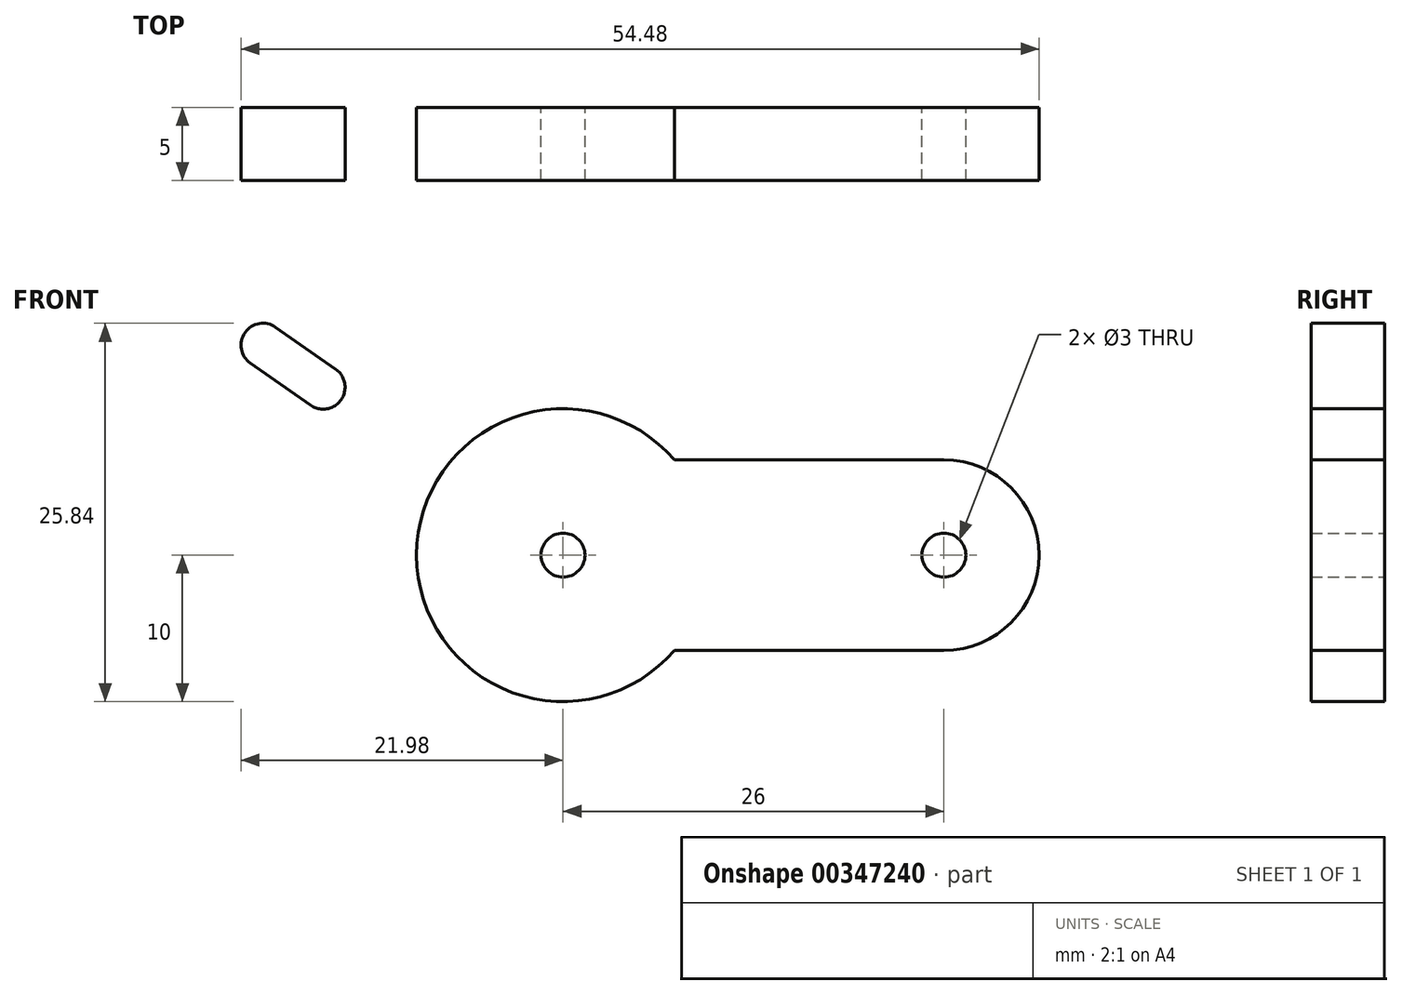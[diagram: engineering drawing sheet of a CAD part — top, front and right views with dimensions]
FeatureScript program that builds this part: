
annotation { "Feature Type Name" : "Feature", "Feature Type Description" : "" }
export const myFeature = defineFeature(function(context is Context, id is Id, definition is map)
    precondition{}
    {
        {
            var Q0;
            Q0=qCreatedBy(makeId("Front.planeOp"),FACE);
            var sketch = newSketch(context, id + "F0", { "sketchPlane" : qUnion([Q0])});
            skLineSegment(sketch, "E0", {"start": v(1.5, 0) * mm, "end": v(26, 0) * mm});
            skLineSegment(sketch, "E1", {"start": v(-1.23, 0.86) * mm, "end": v(-16.38, 11.47) * mm});
            skLineSegment(sketch, "E2", {"start": v(-16.38, 11.47) * mm, "end": v(-20.48, 14.34) * mm});
            skCircle(sketch, "E3", {"center": v(0, 0) * mm, "radius": 1.5 * mm});
            skCircle(sketch, "E4", {"center": v(26, 0) * mm, "radius": 1.5 * mm});
            skArc(sketch, "E5.0.startCap", {"start": v(-15.52, 12.7) * mm, "mid": v(-15.15, 10.61) * mm, "end": v(-17.24, 10.24) * mm});
            skArc(sketch, "E5.0.endCap", {"start": v(-21.34, 13.11) * mm, "mid": v(-21.7, 15.2) * mm, "end": v(-19.62, 15.57) * mm});
            skLineSegment(sketch, "E5.0.left", {"start": v(-17.24, 10.24) * mm, "end": v(-21.34, 13.11) * mm});
            skLineSegment(sketch, "E5.0.right", {"start": v(-15.52, 12.7) * mm, "end": v(-19.62, 15.57) * mm});
            skLineSegment(sketch, "E6.0.left", {"start": v(-9.95, -0.97) * mm, "end": v(-20.11, 6.15) * mm});
            skCircle(sketch, "E7", {"center": v(0, 0) * mm, "radius": 10 * mm});
            skArc(sketch, "E8.0.endCap", {"start": v(26, 6.5) * mm, "mid": v(32.5, 0) * mm, "end": v(26, -6.5) * mm});
            skLineSegment(sketch, "E8.0.right", {"start": v(7.6, -6.5) * mm, "end": v(26, -6.5) * mm});
            skLineSegment(sketch, "E9.trimOffspring", {"start": v(-2.5, 9.68) * mm, "end": v(-12.65, 16.8) * mm});
            skLineSegment(sketch, "E10.trimOffspring", {"start": v(7.6, 6.5) * mm, "end": v(26, 6.5) * mm});
            skLineSegment(sketch, "E11", {"start": v(-20.11, 6.15) * mm, "end": v(-21.34, 7) * mm});
            skLineSegment(sketch, "E12", {"start": v(-12.65, 16.8) * mm, "end": v(-13.88, 17.66) * mm});
            skArc(sketch, "E13", {"start": v(-21.34, 7) * mm, "mid": v(-22.94, 16.06) * mm, "end": v(-13.88, 17.66) * mm});
            skSolve(sketch);
        }
        {
            var Q0;
            Q0=makeQuery(id+"F0.imprint","IMPRINT",FACE,{"disambiguationData":[TD([[makeQuery(id+"F0.imprint","IMPRINT",EDGE,{"derivedFrom":sQuery(id+"F0.wireOp",EDGE,"E5.0.endCap")}),1.0]])]});
            var Q1;
            {var subQ2=sQuery(id+"F0.wireOp",EDGE,"E0");var subQ4=sQuery(id+"F0.wireOp",EDGE,"E3");var subQ5=makeQuery(id+"F0.imprint","INTERSECT",VERTEX,{"derivedFrom":[subQ2,subQ4]});Q1=makeQuery(id+"F0.imprint","IMPRINT",FACE,{"disambiguationData":[TD([[makeQuery(id+"F0.imprint","IMPRINT",EDGE,{"disambiguationData":[TD([[subQ5,-1.0]])],"derivedFrom":subQ2}),1.0]])]});}
            var Q2;
            {var subQ4=sQuery(id+"F0.wireOp",EDGE,"E3");var subQ5=sQuery(id+"F0.wireOp",EDGE,"E0");var subQ6=makeQuery(id+"F0.imprint","INTERSECT",VERTEX,{"derivedFrom":[subQ5,subQ4]});Q2=makeQuery(id+"F0.imprint","IMPRINT",FACE,{"disambiguationData":[TD([[makeQuery(id+"F0.imprint","IMPRINT",EDGE,{"disambiguationData":[TD([[subQ6,-1.0]])],"derivedFrom":subQ5}),-1.0]])]});}
            var Q3;
            Q3=makeQuery(id+"F0.imprint","IMPRINT",FACE,{"disambiguationData":[TD([[makeQuery(id+"F0.imprint","IMPRINT",EDGE,{"derivedFrom":sQuery(id+"F0.wireOp",EDGE,"E4")}),-1.0]])]});
            extrude(context, id + "F1", {"entities" : qUnion([Q0, Q1, Q2, Q3]), "depth" : 5 * mm});
        }
    });
